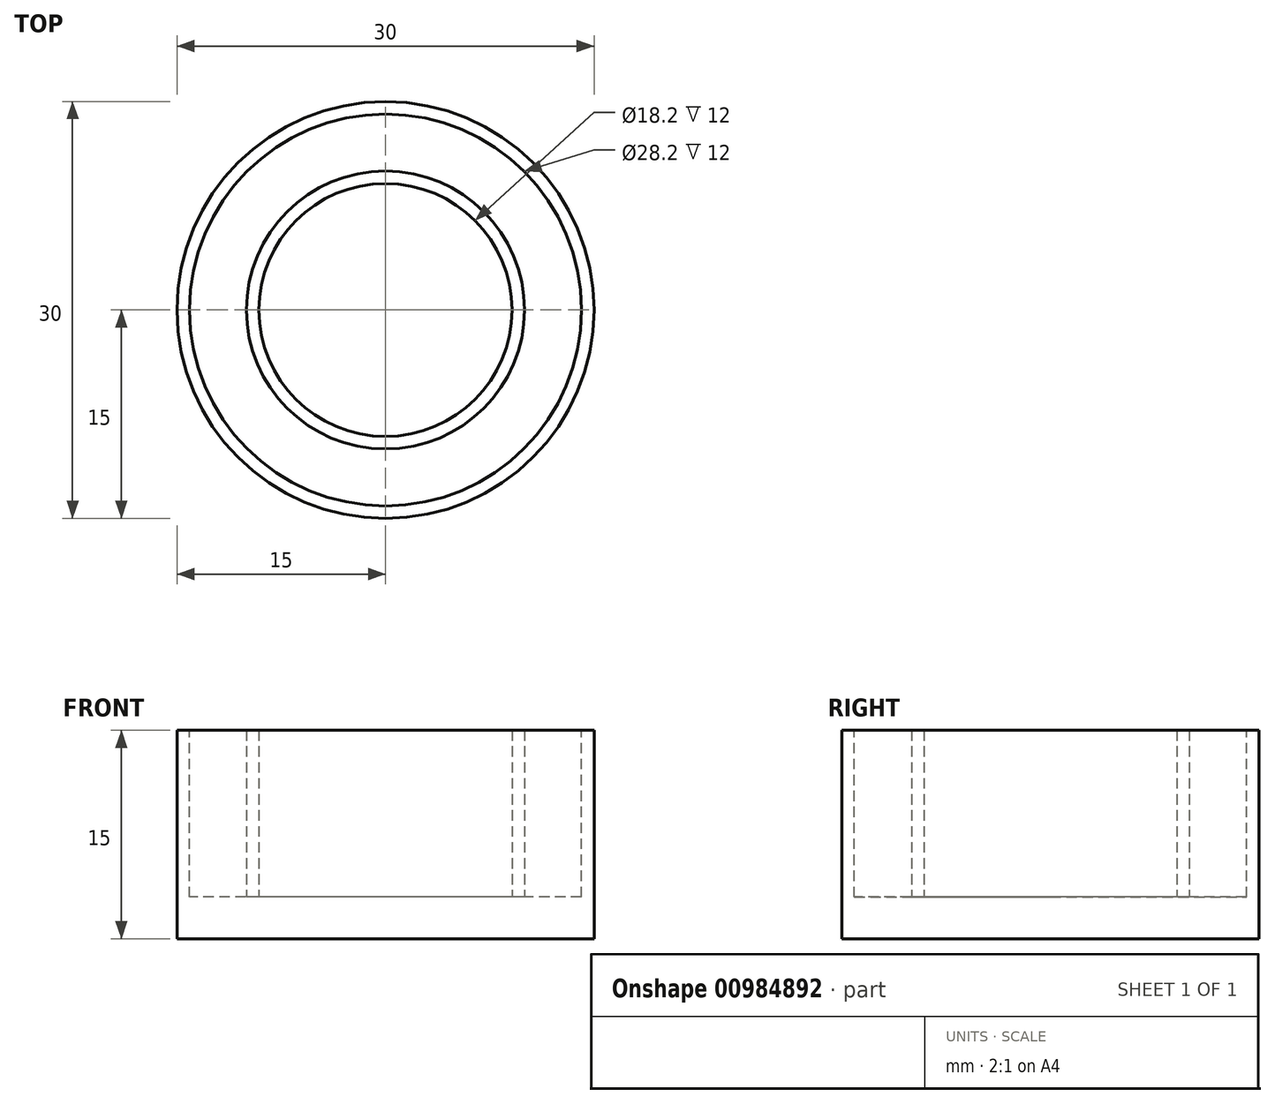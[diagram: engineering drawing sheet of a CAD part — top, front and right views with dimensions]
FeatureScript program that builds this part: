
annotation { "Feature Type Name" : "Feature", "Feature Type Description" : "" }
export const myFeature = defineFeature(function(context is Context, id is Id, definition is map)
    precondition{}
    {
        {
            var Q0;
            Q0=qCreatedBy(makeId("Top.planeOp"),FACE);
            var sketch = newSketch(context, id + "F0", { "sketchPlane" : qUnion([Q0])});
            skCircle(sketch, "E0", {"center": v(0, 0) * mm, "radius": 15 * mm});
            skSolve(sketch);
        }
        {
            var Q0;
            Q0=makeQuery(id+"F0.imprint","IMPRINT",FACE,{"disambiguationData":[TD([[makeQuery(id+"F0.imprint","IMPRINT",EDGE,{"derivedFrom":sQuery(id+"F0.wireOp",EDGE,"E0")}),1.0]])]});
            extrude(context, id + "F1", {"entities" : qUnion([Q0]), "depth" : 15 * mm, "offsetDistance" : 25 * mm});
        }
        {
            var Q0;
            Q0=makeQuery(id+"F1.opExtrude","CAP_FACE",FACE,{"disambiguationData":[OSD([sQuery(id+"F0.wireOp",EDGE,"E0")])],"isStart":false});
            var sketch = newSketch(context, id + "F2", { "sketchPlane" : qUnion([Q0])});
            skCircle(sketch, "E1", {"center": v(0, 0) * mm, "radius": 14.1 * mm});
            skSolve(sketch);
        }
        {
            var Q0;
            Q0=makeQuery(id+"F2.imprint","IMPRINT",FACE,{"disambiguationData":[TD([[makeQuery(id+"F2.imprint","IMPRINT",EDGE,{"derivedFrom":sQuery(id+"F2.wireOp",EDGE,"E1")}),1.0]])]});
            extrude(context, id + "F3", {"entities" : qUnion([Q0]), "operationType" : NewBodyOperationType.REMOVE, "oppositeDirection" : true, "depth" : (15 - 3) * mm, "offsetDistance" : 25 * mm});
        }
        {
            var Q0;
            Q0=makeQuery(id+"F3.boolean.opBoolean","COPY",FACE,{"derivedFrom":makeQuery(id+"F3.opExtrude","CAP_FACE",FACE,{"disambiguationData":[OSD([sQuery(id+"F2.wireOp",EDGE,"E1")])],"isStart":false})});
            var sketch = newSketch(context, id + "F4", { "sketchPlane" : qUnion([Q0])});
            skCircle(sketch, "E2", {"center": v(0, 0) * mm, "radius": 10 * mm});
            skCircle(sketch, "E3", {"center": v(0, 0) * mm, "radius": 9.1 * mm});
            skSolve(sketch);
        }
        {
            var Q0;
            Q0=makeQuery(id+"F4.imprint","IMPRINT",FACE,{"disambiguationData":[TD([[makeQuery(id+"F4.imprint","IMPRINT",EDGE,{"derivedFrom":sQuery(id+"F4.wireOp",EDGE,"E2")}),1.0]])]});
            var Q1;
            Q1=makeQuery(id+"F1.opExtrude","CAP_FACE",FACE,{"disambiguationData":[OSD([sQuery(id+"F0.wireOp",EDGE,"E0")])],"isStart":false});
            extrude(context, id + "F5", {"entities" : qUnion([Q0]), "endBound" : BoundingType.UP_TO_SURFACE, "depth" : 25 * mm, "endBoundEntityFace" : qUnion([Q1]), "offsetDistance" : 25 * mm});
        }
    });
